# Revit family: 3.VIRAJ 45 Recessed-L1200 v1 (1)
name_source: partatom
category: Air Terminals
units: mm (PartAtom-declared; Revit-internal decimal feet)

## family parameters
Cut with Voids When Loaded = No
Host = Face
OmniClass Number = 23.75.70.21.27.11
OmniClass Title = Diffusers, Registers, and Grilles
Part Type = Normal
Room Calculation Point = No
Round Connector Dimension = Use Diameter
Shared = No

## types (1)
- Standard
    Default Elevation = 1200 mm
    Diffuser Half Length = 610 mm
    Diffuser Half Width = 42 mm
    Diffuser Length = 1219 mm
    Diffuser Width = 83 mm  [stored 0.27231 ft]
    Diffuser material = <By Category>
    Duct Height = 150 mm
    Duct Width = 200 mm
    Length 1 = 622 mm  [stored 2.04068 ft]
    Radius = 74 mm
    Slot Number = 2
    Slot Visibility 1 = No
    Slot Visibility 2 = Yes
    Slot Visibility 3 = No
    Slot Visibility 4 = No
    Slot Width = 25 mm  [stored 0.082021 ft]
    Width 1 = 54 mm  [stored 0.177165 ft]
    Width 2 = 21 mm
    Width 3 = 14 mm  [stored 0.0459318 ft]
    Width 4 = 10 mm  [stored 0.0328084 ft]
    Width 5 = 74 mm

note: [stored X ft] marks values corroborated as IEEE doubles in the binary element streams (Revit-internal decimal feet)

## geometry (parser evidence)
native form markers: Sweep x3
no freeform markers — native parametric forms only
